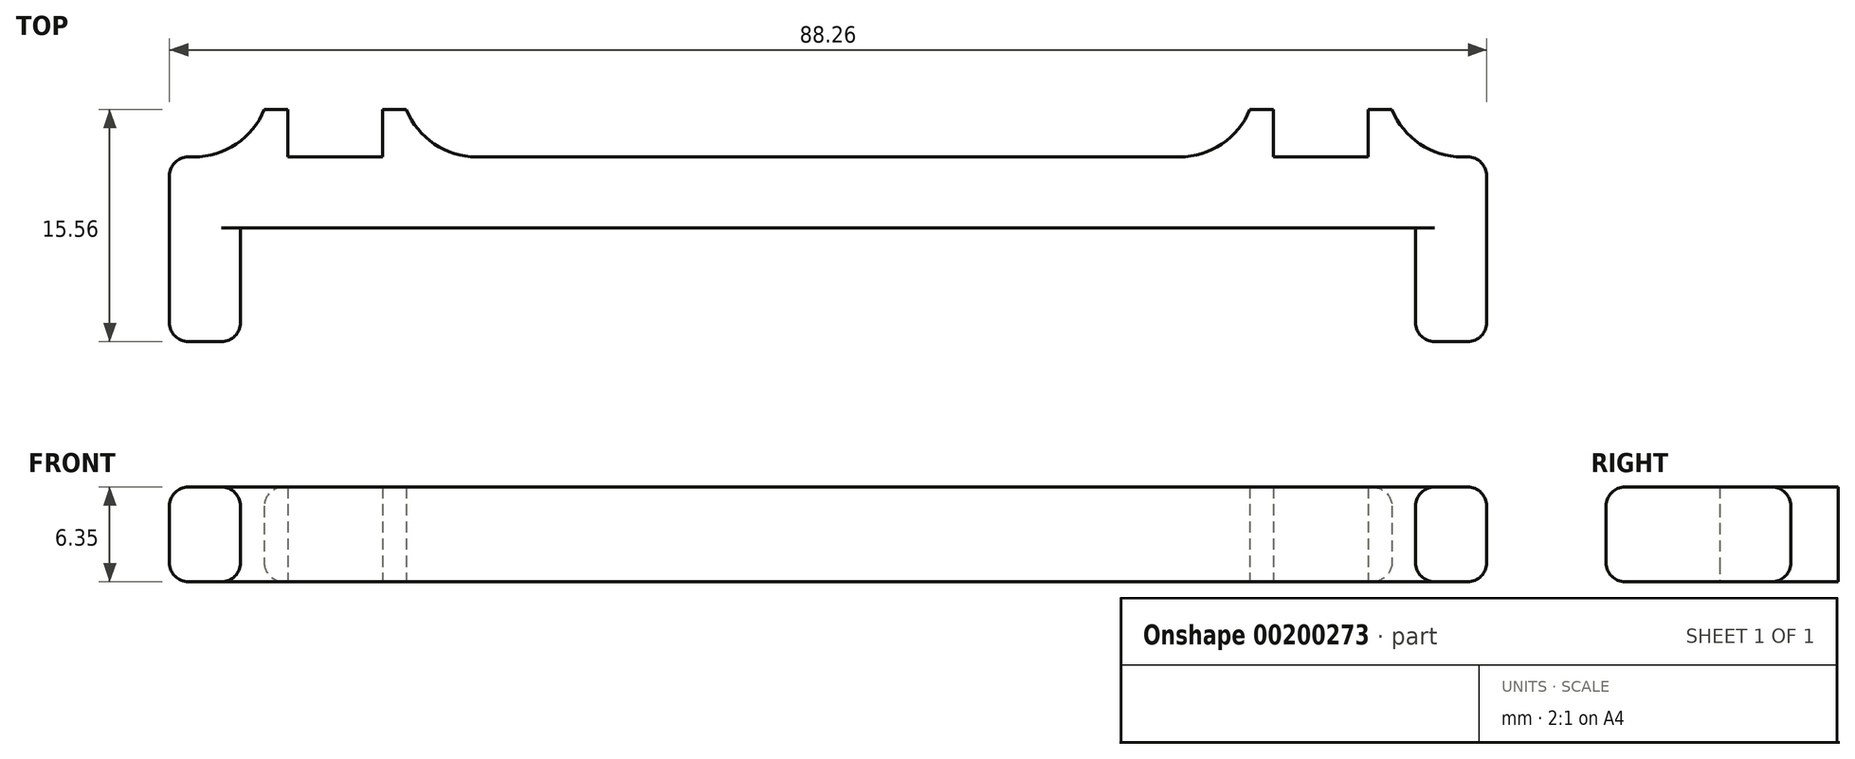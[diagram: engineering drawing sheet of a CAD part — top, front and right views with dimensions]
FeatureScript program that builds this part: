
annotation { "Feature Type Name" : "Feature", "Feature Type Description" : "" }
export const myFeature = defineFeature(function(context is Context, id is Id, definition is map)
    precondition{}
    {
        {
            var Q0;
            Q0=qCreatedBy(makeId("Top.planeOp"),FACE);
            var sketch = newSketch(context, id + "F0", { "sketchPlane" : qUnion([Q0])});
            skLineSegment(sketch, "E0", {"start": v(0, 0) * mm, "end": v(28.26, 0) * mm});
            skLineSegment(sketch, "E1", {"start": v(28.26, 0) * mm, "end": v(28.26, 3.17) * mm});
            skLineSegment(sketch, "E2", {"start": v(28.26, 3.18) * mm, "end": v(29.85, 3.18) * mm});
            skLineSegment(sketch, "E3", {"start": v(29.85, 3.17) * mm, "end": v(29.85, 0) * mm});
            skLineSegment(sketch, "E4", {"start": v(29.85, 0) * mm, "end": v(36.2, 0) * mm});
            skLineSegment(sketch, "E5", {"start": v(36.2, 0) * mm, "end": v(36.2, 3.17) * mm});
            skLineSegment(sketch, "E6", {"start": v(36.2, 3.18) * mm, "end": v(37.78, 3.18) * mm});
            skLineSegment(sketch, "E7", {"start": v(37.78, 3.17) * mm, "end": v(37.78, 0) * mm});
            skLineSegment(sketch, "E8", {"start": v(37.78, 0) * mm, "end": v(44.13, 0) * mm});
            skLineSegment(sketch, "E9", {"start": v(44.13, 0) * mm, "end": v(44.13, -12.38) * mm});
            skLineSegment(sketch, "E10", {"start": v(44.13, -12.38) * mm, "end": v(39.37, -12.38) * mm});
            skLineSegment(sketch, "E11", {"start": v(39.37, -12.38) * mm, "end": v(39.37, -4.76) * mm});
            skLineSegment(sketch, "E12", {"start": v(39.37, -4.76) * mm, "end": v(0, -4.76) * mm});
            skLineSegment(sketch, "E13", {"start": v(0, -4.76) * mm, "end": v(0, 0) * mm});
            skSolve(sketch);
        }
        {
            var Q0;
            Q0=makeQuery(id+"F0.imprint","IMPRINT",FACE,{"disambiguationData":[TD([[makeQuery(id+"F0.imprint","IMPRINT",EDGE,{"derivedFrom":sQuery(id+"F0.wireOp",EDGE,"E0")}),-1.0]])]});
            extrude(context, id + "F1", {"entities" : qUnion([Q0]), "depth" : 6.35 * mm});
        }
        {
            var Q0;
            Q0=makeQuery(id+"F4.opPattern","COPY",EDGE,{"derivedFrom":makeQuery(id+"F1.opExtrude","SWEPT_EDGE",EDGE,{"disambiguationData":[OSD([sQuery(id+"F0.wireOp",EDGE,"E7"),sQuery(id+"F0.wireOp",EDGE,"E8")])]}),"instanceName":"1"});
            var Q1;
            Q1=makeQuery(id+"F4.opPattern","COPY",EDGE,{"derivedFrom":makeQuery(id+"F1.opExtrude","SWEPT_EDGE",EDGE,{"disambiguationData":[OSD([sQuery(id+"F0.wireOp",EDGE,"E0"),sQuery(id+"F0.wireOp",EDGE,"E1")])]}),"instanceName":"1"});
            var Q2;
            Q2=makeQuery(id+"F1.opExtrude","SWEPT_EDGE",EDGE,{"disambiguationData":[OSD([sQuery(id+"F0.wireOp",EDGE,"E0"),sQuery(id+"F0.wireOp",EDGE,"E1")])]});
            var Q3;
            Q3=makeQuery(id+"F1.opExtrude","SWEPT_EDGE",EDGE,{"disambiguationData":[OSD([sQuery(id+"F0.wireOp",EDGE,"E7"),sQuery(id+"F0.wireOp",EDGE,"E8")])]});
            fillet(context, id + "F2", {"entities" : qUnion([Q0, Q1, Q2, Q3]), "radius" : 5.08 * mm, "tangentPropagation" : true, "allowEdgeOverflow" : false});
        }
        {
            var Q0;
            Q0=makeQuery(id+"F1.opExtrude","CAP_EDGE",EDGE,{"disambiguationData":[OSD([sQuery(id+"F0.wireOp",EDGE,"E11")])],"isStart":true});
            var Q1;
            Q1=makeQuery(id+"F1.opExtrude","CAP_EDGE",EDGE,{"disambiguationData":[OSD([sQuery(id+"F0.wireOp",EDGE,"E9")])],"isStart":false});
            var Q2;
            Q2=makeQuery(id+"F1.opExtrude","CAP_EDGE",EDGE,{"disambiguationData":[OSD([sQuery(id+"F0.wireOp",EDGE,"E10")])],"isStart":false});
            var Q3;
            Q3=makeQuery(id+"F1.opExtrude","SWEPT_EDGE",EDGE,{"disambiguationData":[OSD([sQuery(id+"F0.wireOp",EDGE,"E9"),sQuery(id+"F0.wireOp",EDGE,"E10")])]});
            var Q4;
            Q4=makeQuery(id+"F1.opExtrude","SWEPT_EDGE",EDGE,{"disambiguationData":[OSD([sQuery(id+"F0.wireOp",EDGE,"E10"),sQuery(id+"F0.wireOp",EDGE,"E11")])]});
            var Q5;
            Q5=makeQuery(id+"F1.opExtrude","CAP_EDGE",EDGE,{"disambiguationData":[OSD([sQuery(id+"F0.wireOp",EDGE,"E10")])],"isStart":true});
            var Q6;
            Q6=makeQuery(id+"F1.opExtrude","CAP_EDGE",EDGE,{"disambiguationData":[OSD([sQuery(id+"F0.wireOp",EDGE,"E11")])],"isStart":false});
            var Q7;
            Q7=makeQuery(id+"F1.opExtrude","CAP_EDGE",EDGE,{"disambiguationData":[OSD([sQuery(id+"F0.wireOp",EDGE,"E9")])],"isStart":true});
            var Q8;
            {var subQ0=sQuery(id+"F0.wireOp",EDGE,"E8");var subQ1=sQuery(id+"F0.wireOp",EDGE,"E7");Q8=makeQuery(id+"F2.opFillet","BLEND_EDGE",EDGE,{"blendedFrom":[makeQuery(id+"F1.opExtrude","SWEPT_EDGE",EDGE,{"disambiguationData":[OSD([subQ1,subQ0])]}),makeQuery(id+"F1.opExtrude","CAP_FACE",FACE,{"disambiguationData":[OSD([sQuery(id+"F0.wireOp",EDGE,"E0"),sQuery(id+"F0.wireOp",EDGE,"E1"),sQuery(id+"F0.wireOp",EDGE,"E2"),sQuery(id+"F0.wireOp",EDGE,"E3"),sQuery(id+"F0.wireOp",EDGE,"E4"),sQuery(id+"F0.wireOp",EDGE,"E5"),sQuery(id+"F0.wireOp",EDGE,"E6"),subQ1,subQ0,sQuery(id+"F0.wireOp",EDGE,"E9"),sQuery(id+"F0.wireOp",EDGE,"E10"),sQuery(id+"F0.wireOp",EDGE,"E11"),sQuery(id+"F0.wireOp",EDGE,"E12"),sQuery(id+"F0.wireOp",EDGE,"E13")])],"isStart":false})],"blendedInto":[makeQuery(id+"F1.opExtrude","CAP_FACE",FACE,{"disambiguationData":[OSD([sQuery(id+"F0.wireOp",EDGE,"E0"),sQuery(id+"F0.wireOp",EDGE,"E1"),sQuery(id+"F0.wireOp",EDGE,"E2"),sQuery(id+"F0.wireOp",EDGE,"E3"),sQuery(id+"F0.wireOp",EDGE,"E4"),sQuery(id+"F0.wireOp",EDGE,"E5"),sQuery(id+"F0.wireOp",EDGE,"E6"),subQ1,subQ0,sQuery(id+"F0.wireOp",EDGE,"E9"),sQuery(id+"F0.wireOp",EDGE,"E10"),sQuery(id+"F0.wireOp",EDGE,"E11"),sQuery(id+"F0.wireOp",EDGE,"E12"),sQuery(id+"F0.wireOp",EDGE,"E13")])],"isStart":false})]});}
            var Q9;
            {var subQ0=sQuery(id+"F0.wireOp",EDGE,"E8");var subQ1=sQuery(id+"F0.wireOp",EDGE,"E7");Q9=makeQuery(id+"F2.opFillet","BLEND_EDGE",EDGE,{"blendedFrom":[makeQuery(id+"F1.opExtrude","SWEPT_EDGE",EDGE,{"disambiguationData":[OSD([subQ1,subQ0])]}),makeQuery(id+"F1.opExtrude","CAP_FACE",FACE,{"disambiguationData":[OSD([sQuery(id+"F0.wireOp",EDGE,"E0"),sQuery(id+"F0.wireOp",EDGE,"E1"),sQuery(id+"F0.wireOp",EDGE,"E2"),sQuery(id+"F0.wireOp",EDGE,"E3"),sQuery(id+"F0.wireOp",EDGE,"E4"),sQuery(id+"F0.wireOp",EDGE,"E5"),sQuery(id+"F0.wireOp",EDGE,"E6"),subQ1,subQ0,sQuery(id+"F0.wireOp",EDGE,"E9"),sQuery(id+"F0.wireOp",EDGE,"E10"),sQuery(id+"F0.wireOp",EDGE,"E11"),sQuery(id+"F0.wireOp",EDGE,"E12"),sQuery(id+"F0.wireOp",EDGE,"E13")])],"isStart":true})],"blendedInto":[makeQuery(id+"F1.opExtrude","CAP_FACE",FACE,{"disambiguationData":[OSD([sQuery(id+"F0.wireOp",EDGE,"E0"),sQuery(id+"F0.wireOp",EDGE,"E1"),sQuery(id+"F0.wireOp",EDGE,"E2"),sQuery(id+"F0.wireOp",EDGE,"E3"),sQuery(id+"F0.wireOp",EDGE,"E4"),sQuery(id+"F0.wireOp",EDGE,"E5"),sQuery(id+"F0.wireOp",EDGE,"E6"),subQ1,subQ0,sQuery(id+"F0.wireOp",EDGE,"E9"),sQuery(id+"F0.wireOp",EDGE,"E10"),sQuery(id+"F0.wireOp",EDGE,"E11"),sQuery(id+"F0.wireOp",EDGE,"E12"),sQuery(id+"F0.wireOp",EDGE,"E13")])],"isStart":true})]});}
            var Q10;
            Q10=makeQuery(id+"F1.opExtrude","CAP_EDGE",EDGE,{"disambiguationData":[OSD([sQuery(id+"F0.wireOp",EDGE,"E8")])],"isStart":false});
            var Q11;
            Q11=makeQuery(id+"F1.opExtrude","CAP_EDGE",EDGE,{"disambiguationData":[OSD([sQuery(id+"F0.wireOp",EDGE,"E8")])],"isStart":true});
            var Q12;
            Q12=makeQuery(id+"F1.opExtrude","SWEPT_EDGE",EDGE,{"disambiguationData":[OSD([sQuery(id+"F0.wireOp",EDGE,"E8"),sQuery(id+"F0.wireOp",EDGE,"E9")])]});
            fillet(context, id + "F3", {"entities" : qUnion([Q0, Q1, Q2, Q3, Q4, Q5, Q6, Q7, Q8, Q9, Q10, Q11, Q12]), "radius" : 1.27 * mm, "allowEdgeOverflow" : false});
        }
        {
            var Q0;
            Q0=makeQuery(id+"F1.opExtrude","SWEPT_BODY",BODY,{"disambiguationData":[OSD([sQuery(id+"F0.wireOp",EDGE,"E0"),sQuery(id+"F0.wireOp",EDGE,"E1"),sQuery(id+"F0.wireOp",EDGE,"E2"),sQuery(id+"F0.wireOp",EDGE,"E3"),sQuery(id+"F0.wireOp",EDGE,"E4"),sQuery(id+"F0.wireOp",EDGE,"E5"),sQuery(id+"F0.wireOp",EDGE,"E6"),sQuery(id+"F0.wireOp",EDGE,"E7"),sQuery(id+"F0.wireOp",EDGE,"E8"),sQuery(id+"F0.wireOp",EDGE,"E9"),sQuery(id+"F0.wireOp",EDGE,"E10"),sQuery(id+"F0.wireOp",EDGE,"E11"),sQuery(id+"F0.wireOp",EDGE,"E12"),sQuery(id+"F0.wireOp",EDGE,"E13")])]});
            var Q1;
            Q1=qCreatedBy(makeId("Right.planeOp"),FACE);
            mirror(context, id + "F4", {"operationType" : NewBodyOperationType.ADD, "entities" : qUnion([Q0]), "mirrorPlane" : qUnion([Q1])});
        }
    });
